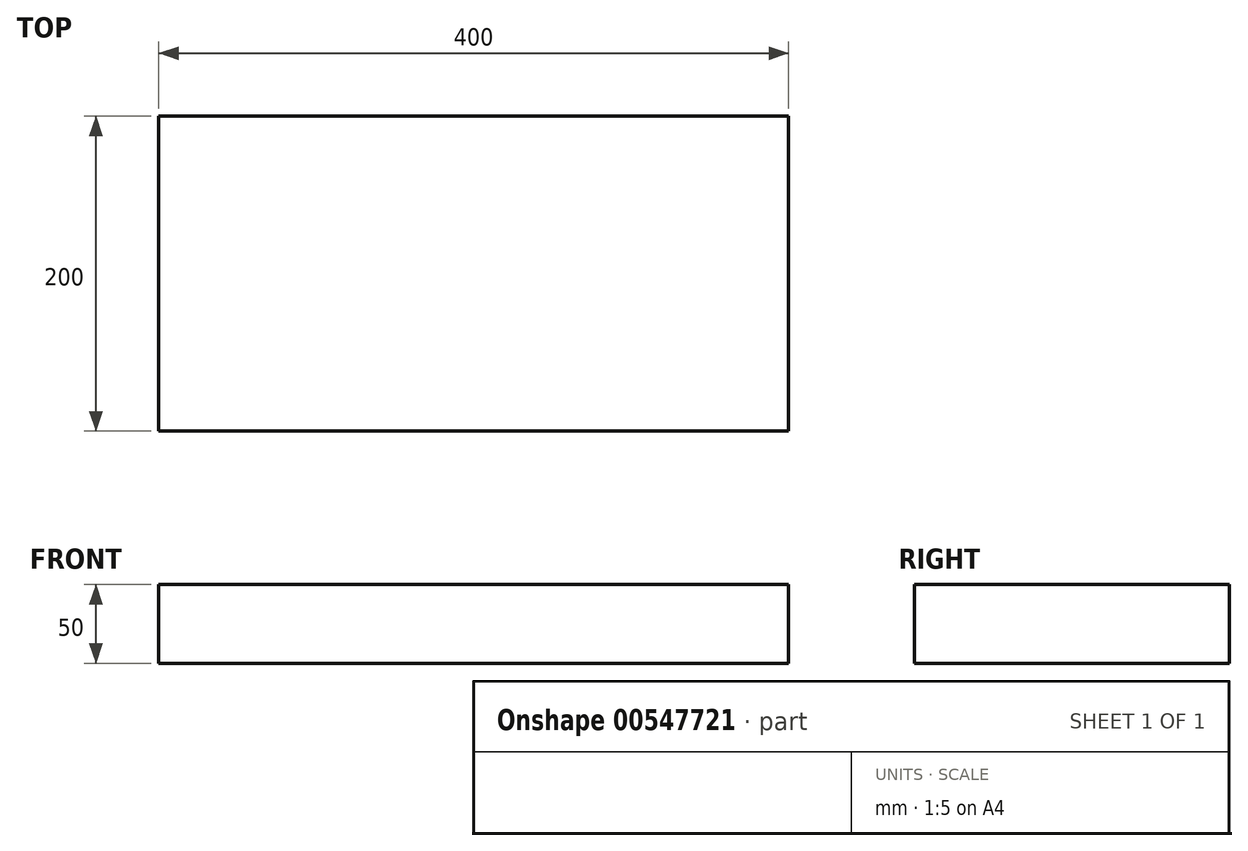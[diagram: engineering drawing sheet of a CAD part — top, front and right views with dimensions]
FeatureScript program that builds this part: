
annotation { "Feature Type Name" : "Feature", "Feature Type Description" : "" }
export const myFeature = defineFeature(function(context is Context, id is Id, definition is map)
    precondition{}
    {
        {
            var Q0;
            Q0=qCreatedBy(makeId("Top.planeOp"),FACE);
            var sketch = newSketch(context, id + "F0", { "sketchPlane" : qUnion([Q0])});
            skLineSegment(sketch, "E0.bottom", {"start": v(200, 100) * mm, "end": v(-200, 100) * mm});
            skLineSegment(sketch, "E0.top", {"start": v(200, -100) * mm, "end": v(-200, -100) * mm});
            skLineSegment(sketch, "E0.left", {"start": v(200, 100) * mm, "end": v(200, -100) * mm});
            skLineSegment(sketch, "E0.right", {"start": v(-200, 100) * mm, "end": v(-200, -100) * mm});
            skPoint(sketch, "E0.middle", {"position": v(0, 0) * mm});
            skSolve(sketch);
        }
        {
            var Q0;
            Q0 = qSketchRegion(id + "F0", true);
            extrude(context, id + "F1", {"entities" : qUnion([Q0]), "depth" : 50 * mm, "offsetDistance" : 25 * mm});
        }
    });
